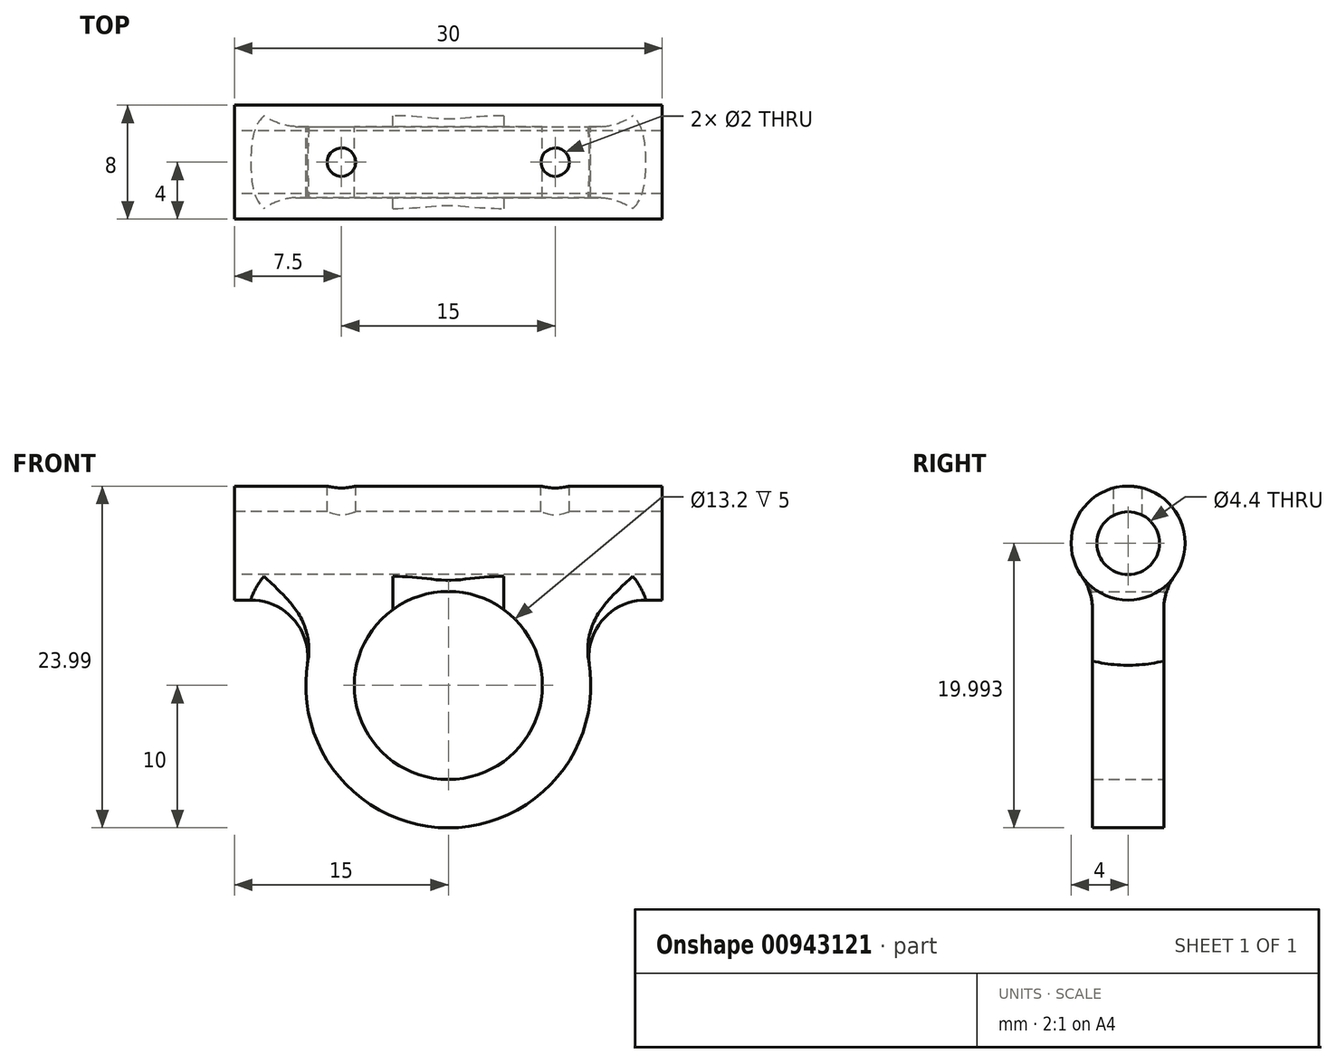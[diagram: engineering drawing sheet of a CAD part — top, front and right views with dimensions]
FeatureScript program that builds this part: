
annotation { "Feature Type Name" : "Feature", "Feature Type Description" : "" }
export const myFeature = defineFeature(function(context is Context, id is Id, definition is map)
    precondition{}
    {
        {
            var Q0;
            Q0=qCreatedBy(makeId("Front.planeOp"),FACE);
            var sketch = newSketch(context, id + "F0", { "sketchPlane" : qUnion([Q0])});
            skCircle(sketch, "E0", {"center": v(0, 0) * mm, "radius": 6.6 * mm});
            skCircle(sketch, "E1", {"center": v(0, 0) * mm, "radius": 10 * mm});
            skSolve(sketch);
        }
        {
            var Q0;
            Q0=qSketchRegion(id+"F0",true);
            extrude(context, id + "F1", {"entities" : qUnion([Q0]), "endBound" : BoundingType.SYMMETRIC, "depth" : 5 * mm, "offsetDistance" : 25 * mm});
        }
        {
            var Q0;
            Q0=qCreatedBy(makeId("Right.planeOp"),FACE);
            var sketch = newSketch(context, id + "F2", { "sketchPlane" : qUnion([Q0])});
            skCircle(sketch, "E2", {"center": v(0, 10) * mm, "radius": 2.2 * mm});
            skCircle(sketch, "E3", {"center": v(0, 10) * mm, "radius": 4 * mm});
            skSolve(sketch);
        }
        {
            var Q0;
            Q0=qSketchRegion(id+"F2",true);
            extrude(context, id + "F3", {"entities" : qUnion([Q0]), "operationType" : NewBodyOperationType.ADD, "endBound" : BoundingType.SYMMETRIC, "depth" : 30 * mm, "offsetDistance" : 25 * mm});
        }
        {
            var Q0;
            Q0=makeQuery(id+"F2.imprint","IMPRINT",FACE,{"disambiguationData":[TD([[makeQuery(id+"F2.imprint","IMPRINT",EDGE,{"derivedFrom":sQuery(id+"F2.wireOp",EDGE,"E2")}),1.0]])]});
            extrude(context, id + "F4", {"entities" : qUnion([Q0]), "operationType" : NewBodyOperationType.REMOVE, "endBound" : BoundingType.SYMMETRIC, "depth" : 25 * mm, "offsetDistance" : 25 * mm});
        }
        {
            var Q0;
            Q0=makeQuery(id+"F3.boolean.opBoolean","INTERSECT",EDGE,{"disambiguationData":[OD(0.0)],"derivedFrom":[makeQuery(id+"F1.opExtrude","SWEPT_FACE",FACE,{"disambiguationData":[OSD([sQuery(id+"F0.wireOp",EDGE,"E1")])]}),makeQuery(id+"F3.opExtrude","SWEPT_FACE",FACE,{"disambiguationData":[OSD([sQuery(id+"F2.wireOp",EDGE,"E3")])]})]});
            var Q1;
            Q1=makeQuery(id+"F3.boolean.opBoolean","INTERSECT",EDGE,{"derivedFrom":[makeQuery(id+"F1.opExtrude","CAP_FACE",FACE,{"disambiguationData":[OSD([sQuery(id+"F0.wireOp",EDGE,"E0"),sQuery(id+"F0.wireOp",EDGE,"E1")])],"isStart":true}),makeQuery(id+"F3.opExtrude","SWEPT_FACE",FACE,{"disambiguationData":[OSD([sQuery(id+"F2.wireOp",EDGE,"E3")])]})]});
            var Q2;
            Q2=makeQuery(id+"F3.boolean.opBoolean","INTERSECT",EDGE,{"derivedFrom":[makeQuery(id+"F1.opExtrude","CAP_FACE",FACE,{"disambiguationData":[OSD([sQuery(id+"F0.wireOp",EDGE,"E0"),sQuery(id+"F0.wireOp",EDGE,"E1")])],"isStart":false}),makeQuery(id+"F3.opExtrude","SWEPT_FACE",FACE,{"disambiguationData":[OSD([sQuery(id+"F2.wireOp",EDGE,"E3")])]})]});
            var Q3;
            Q3=makeQuery(id+"F3.boolean.opBoolean","INTERSECT",EDGE,{"disambiguationData":[OD(1.0)],"derivedFrom":[makeQuery(id+"F1.opExtrude","SWEPT_FACE",FACE,{"disambiguationData":[OSD([sQuery(id+"F0.wireOp",EDGE,"E1")])]}),makeQuery(id+"F3.opExtrude","SWEPT_FACE",FACE,{"disambiguationData":[OSD([sQuery(id+"F2.wireOp",EDGE,"E3")])]})]});
            fillet(context, id + "F5", {"entities" : qUnion([Q0, Q1, Q2, Q3]), "radius" : 4 * mm, "tangentPropagation" : true, "allowEdgeOverflow" : false});
        }
        {
            var Q0;
            Q0=makeQuery(id+"F0.imprint","IMPRINT",FACE,{"disambiguationData":[TD([[makeQuery(id+"F0.imprint","IMPRINT",EDGE,{"derivedFrom":sQuery(id+"F0.wireOp",EDGE,"E0")}),1.0]])]});
            extrude(context, id + "F6", {"entities" : qUnion([Q0]), "operationType" : NewBodyOperationType.REMOVE, "endBound" : BoundingType.SYMMETRIC, "oppositeDirection" : true, "depth" : 20 * mm, "offsetDistance" : 25 * mm});
        }
        {
            var Q0;
            Q0=qCreatedBy(makeId("Top.planeOp"),FACE);
            cPlane(context, id + "F7", {"entities" : qUnion([Q0]), "cplaneType" : CPlaneType.OFFSET, "offset" : 17.4 * mm, "width" : 150 * mm, "height" : 150 * mm});
        }
        {
            var Q0;
            Q0=qCreatedBy(id+"F7.planeOp",FACE);
            var sketch = newSketch(context, id + "F8", { "sketchPlane" : qUnion([Q0])});
            skPoint(sketch, "E4", {"position": v(-7.5, 0) * mm});
            skPoint(sketch, "E5", {"position": v(7.5, 0) * mm});
            skLineSegment(sketch, "E6", {"start": v(0, 0) * mm, "end": v(-15, 0) * mm, "construction": true});
            skSolve(sketch);
        }
        {
            var Q0;
            Q0=sQuery(id+"F8.wireOp",VERTEX,"E4");
            var Q1;
            Q1=sQuery(id+"F8.wireOp",VERTEX,"E5");
            var Q2;
            Q2=makeQuery(id+"F1.opExtrude","SWEPT_BODY",BODY,{"disambiguationData":[OSD([sQuery(id+"F0.wireOp",EDGE,"E0"),sQuery(id+"F0.wireOp",EDGE,"E1")])]});
            hole(context, id + "F9", {"style" : HoleStyle.SIMPLE, "endStyle" : HoleEndStyle.BLIND, "holeDiameter" : 2 * mm, "majorDiameter" : 5 * mm, "holeDepth" : 5 * mm, "isTappedThrough" : true, "tappedDepth" : 12 * mm, "tapClearance" : 3, "locations" : qUnion([Q0, Q1]), "scope" : qUnion([Q2])});
        }
    });
